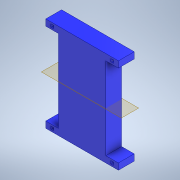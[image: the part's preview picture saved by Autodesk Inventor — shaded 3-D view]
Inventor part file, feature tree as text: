
AUTODESK INVENTOR PART (.ipt)
format: ipt  version: 2020 (Build 240168000, 168)  size: 145,408 bytes
history: native  units: mm
features: extrude x3, sketch x3, plane x2, mirror x2
ambient origin geometry x8: Origin, YZ Plane, XZ Plane, XY Plane, X Axis, Y Axis, Z Axis, Center Point
bodies: Solid1 (feature_tree)
feature tree (10):
  extrude  "Extrusion1"  Depth=600.0mm
  extrude  "Extrusion2"  Depth=80.0mm
  extrude  "Extrusion3"  Depth=100.0mm TaperAngle=0.0deg
  plane  "Work Plane1"
  mirror  "Mirror1"
  plane  "Work Plane2"
  mirror  "Mirror2"
  sketch  "Sketch1"  dims[d0=300.0mm d1=600.0mm]
  sketch  "Sketch2"  dims[d2=100.0mm d3=0.0mm d4=80.0mm]
  sketch  "Sketch3"  dims[d5=40.0mm d6=100.0mm d7=0.0mm d8=24.0mm d9=18.3mm d10=100.0mm d11=0.0mm]
